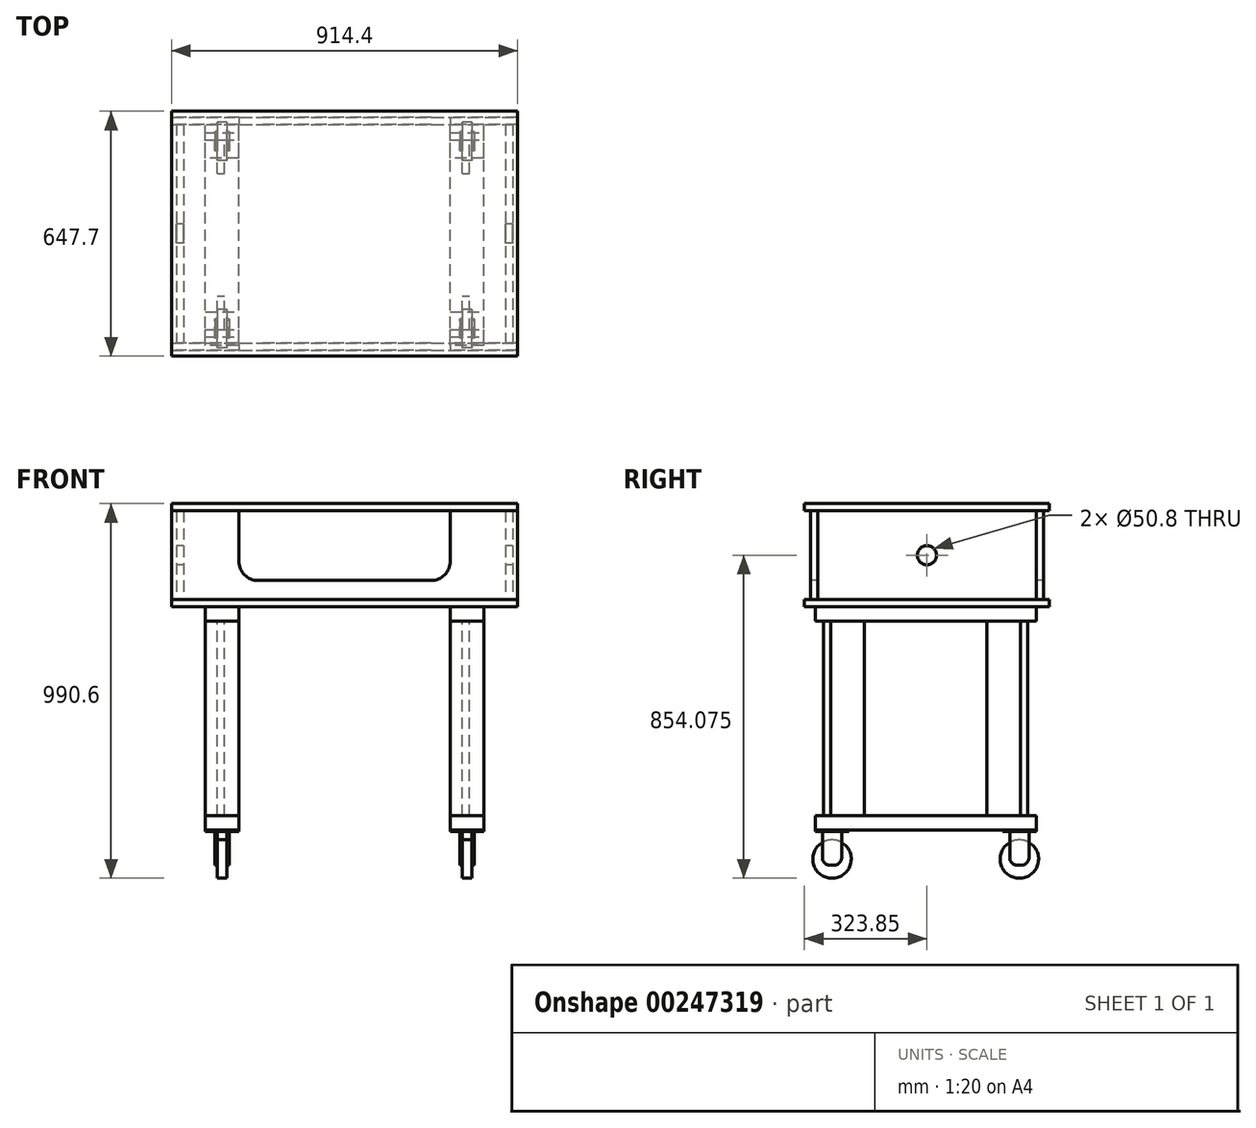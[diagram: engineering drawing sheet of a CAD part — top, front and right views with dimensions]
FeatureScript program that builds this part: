
annotation { "Feature Type Name" : "Feature", "Feature Type Description" : "" }
export const myFeature = defineFeature(function(context is Context, id is Id, definition is map)
    precondition{}
    {
        {
            var Q0;
            Q0=qCreatedBy(makeId("Right.planeOp"),FACE);
            var sketch = newSketch(context, id + "F0", { "sketchPlane" : qUnion([Q0])});
            skLineSegment(sketch, "E0.bottom", {"start": v(0, 0) * mm, "end": v(647.7, 0) * mm});
            skLineSegment(sketch, "E0.top", {"start": v(0, 19.05) * mm, "end": v(647.7, 19.05) * mm});
            skLineSegment(sketch, "E0.left", {"start": v(0, 0) * mm, "end": v(0, 19.05) * mm});
            skLineSegment(sketch, "E0.right", {"start": v(647.7, 0) * mm, "end": v(647.7, 19.05) * mm});
            skSolve(sketch);
        }
        {
            var Q0;
            Q0=makeQuery(id+"F0.imprint","IMPRINT",FACE,{"disambiguationData":[TD([[makeQuery(id+"F0.imprint","IMPRINT",EDGE,{"derivedFrom":sQuery(id+"F0.wireOp",EDGE,"E0.bottom")}),1.0]])]});
            extrude(context, id + "F1", {"entities" : qUnion([Q0]), "oppositeDirection" : true, "depth" : 914.4 * mm});
        }
        {
            var Q0;
            Q0=qCreatedBy(makeId("Top.planeOp"),FACE);
            var sketch = newSketch(context, id + "F2", { "sketchPlane" : qUnion([Q0])});
            skLineSegment(sketch, "E1.bottom", {"start": v(0, 0) * mm, "end": v(-88.9, 0) * mm});
            skLineSegment(sketch, "E1.top", {"start": v(0, 584.2) * mm, "end": v(-88.9, 584.2) * mm});
            skLineSegment(sketch, "E1.left", {"start": v(0, 0) * mm, "end": v(0, 584.2) * mm});
            skLineSegment(sketch, "E1.right", {"start": v(-88.9, 0) * mm, "end": v(-88.9, 584.2) * mm});
            skSolve(sketch);
        }
        {
            var Q0;
            Q0=makeQuery(id+"F2.imprint","IMPRINT",FACE,{"disambiguationData":[TD([[makeQuery(id+"F2.imprint","IMPRINT",EDGE,{"derivedFrom":sQuery(id+"F2.wireOp",EDGE,"E1.bottom")}),-1.0]])]});
            extrude(context, id + "F3", {"entities" : qUnion([Q0]), "oppositeDirection" : true, "depth" : 38.1 * mm});
        }
        {
            var Q0;
            Q0=makeQuery(id+"F3.opExtrude","SWEPT_FACE",FACE,{"disambiguationData":[OSD([sQuery(id+"F2.wireOp",EDGE,"E1.left")])]});
            var sketch = newSketch(context, id + "F4", { "sketchPlane" : qUnion([Q0])});
            skLineSegment(sketch, "E2.bottom", {"start": v(50.8, -38.1) * mm, "end": v(69.85, -38.1) * mm});
            skLineSegment(sketch, "E2.top", {"start": v(50.8, -552.45) * mm, "end": v(69.85, -552.45) * mm});
            skLineSegment(sketch, "E2.left", {"start": v(50.8, -38.1) * mm, "end": v(50.8, -552.45) * mm});
            skLineSegment(sketch, "E2.right", {"start": v(69.85, -38.1) * mm, "end": v(69.85, -552.45) * mm});
            skSolve(sketch);
        }
        {
            var Q0;
            Q0=makeQuery(id+"F4.imprint","IMPRINT",FACE,{"disambiguationData":[TD([[makeQuery(id+"F4.imprint","IMPRINT",EDGE,{"derivedFrom":sQuery(id+"F4.wireOp",EDGE,"E2.bottom")}),-1.0]])]});
            extrude(context, id + "F5", {"entities" : qUnion([Q0]), "oppositeDirection" : true, "depth" : 88.9 * mm});
        }
        {
            var Q0;
            Q0=makeQuery(id+"F5.opExtrude","SWEPT_FACE",FACE,{"disambiguationData":[OSD([sQuery(id+"F4.wireOp",EDGE,"E2.bottom")])]});
            var sketch = newSketch(context, id + "F6", { "sketchPlane" : qUnion([Q0])});
            skLineSegment(sketch, "E3.bottom", {"start": v(-57.48, 69.85) * mm, "end": v(-38.43, 69.85) * mm});
            skLineSegment(sketch, "E3.top", {"start": v(-57.48, 158.75) * mm, "end": v(-38.43, 158.75) * mm});
            skLineSegment(sketch, "E3.left", {"start": v(-57.48, 69.85) * mm, "end": v(-57.48, 158.75) * mm});
            skLineSegment(sketch, "E3.right", {"start": v(-38.43, 69.85) * mm, "end": v(-38.43, 158.75) * mm});
            skSolve(sketch);
        }
        {
            var Q0;
            Q0=makeQuery(id+"F6.imprint","IMPRINT",FACE,{"disambiguationData":[TD([[makeQuery(id+"F6.imprint","IMPRINT",EDGE,{"derivedFrom":sQuery(id+"F6.wireOp",EDGE,"E3.bottom")}),1.0]])]});
            extrude(context, id + "F7", {"entities" : qUnion([Q0]), "oppositeDirection" : true, "depth" : 514.35 * mm});
        }
        {
            var Q0;
            Q0=makeQuery(id+"F5.opExtrude","SWEPT_BODY",BODY,{"disambiguationData":[OSD([sQuery(id+"F4.wireOp",EDGE,"E2.bottom"),sQuery(id+"F4.wireOp",EDGE,"E2.top"),sQuery(id+"F4.wireOp",EDGE,"E2.left"),sQuery(id+"F4.wireOp",EDGE,"E2.right")])]});
            transform(context, id + "F8", {"entities" : qUnion([Q0]), "transformType" : TransformType.TRANSLATION_3D, "dx" : 0 * mm, "dy" : 520.7 * mm, "dz" : 0 * mm, "makeCopy" : true});
        }
        {
            var Q0;
            Q0=makeQuery(id+"F7.opExtrude","SWEPT_BODY",BODY,{"disambiguationData":[OSD([sQuery(id+"F6.wireOp",EDGE,"E3.bottom"),sQuery(id+"F6.wireOp",EDGE,"E3.top"),sQuery(id+"F6.wireOp",EDGE,"E3.left"),sQuery(id+"F6.wireOp",EDGE,"E3.right")])]});
            transform(context, id + "F9", {"entities" : qUnion([Q0]), "transformType" : TransformType.TRANSLATION_3D, "dx" : 0 * mm, "dy" : 412.75 * mm, "dz" : 0 * mm, "makeCopy" : true});
        }
        {
            var Q0;
            Q0=makeQuery(id+"F3.opExtrude","SWEPT_BODY",BODY,{"disambiguationData":[OSD([sQuery(id+"F2.wireOp",EDGE,"E1.bottom"),sQuery(id+"F2.wireOp",EDGE,"E1.top"),sQuery(id+"F2.wireOp",EDGE,"E1.left"),sQuery(id+"F2.wireOp",EDGE,"E1.right")])]});
            transform(context, id + "F10", {"entities" : qUnion([Q0]), "transformType" : TransformType.TRANSLATION_3D, "dx" : -647.7 * mm, "dy" : 0 * mm, "dz" : 0 * mm, "makeCopy" : true});
        }
        {
            var Q0;
            Q0=makeQuery(id+"F5.opExtrude","SWEPT_BODY",BODY,{"disambiguationData":[OSD([sQuery(id+"F4.wireOp",EDGE,"E2.bottom"),sQuery(id+"F4.wireOp",EDGE,"E2.top"),sQuery(id+"F4.wireOp",EDGE,"E2.left"),sQuery(id+"F4.wireOp",EDGE,"E2.right")])]});
            transform(context, id + "F11", {"entities" : qUnion([Q0]), "transformType" : TransformType.TRANSLATION_3D, "dx" : -647.7 * mm, "dy" : 0 * mm, "dz" : 0 * mm, "makeCopy" : true});
        }
        {
            var Q0;
            Q0=makeQuery(id+"F8.opPattern","COPY",BODY,{"derivedFrom":makeQuery(id+"F5.opExtrude","SWEPT_BODY",BODY,{"disambiguationData":[OSD([sQuery(id+"F4.wireOp",EDGE,"E2.bottom"),sQuery(id+"F4.wireOp",EDGE,"E2.top"),sQuery(id+"F4.wireOp",EDGE,"E2.left"),sQuery(id+"F4.wireOp",EDGE,"E2.right")])]}),"instanceName":"1"});
            transform(context, id + "F12", {"entities" : qUnion([Q0]), "transformType" : TransformType.TRANSLATION_3D, "dx" : -647.7 * mm, "dy" : 0 * mm, "dz" : 0 * mm, "makeCopy" : true});
        }
        {
            var Q0;
            Q0=makeQuery(id+"F9.opPattern","COPY",BODY,{"derivedFrom":makeQuery(id+"F7.opExtrude","SWEPT_BODY",BODY,{"disambiguationData":[OSD([sQuery(id+"F6.wireOp",EDGE,"E3.bottom"),sQuery(id+"F6.wireOp",EDGE,"E3.top"),sQuery(id+"F6.wireOp",EDGE,"E3.left"),sQuery(id+"F6.wireOp",EDGE,"E3.right")])]}),"instanceName":"1"});
            transform(context, id + "F13", {"entities" : qUnion([Q0]), "transformType" : TransformType.TRANSLATION_3D, "dx" : -647.7 * mm, "dy" : 0 * mm, "dz" : 0 * mm, "makeCopy" : true});
        }
        {
            var Q0;
            Q0=makeQuery(id+"F7.opExtrude","SWEPT_BODY",BODY,{"disambiguationData":[OSD([sQuery(id+"F6.wireOp",EDGE,"E3.bottom"),sQuery(id+"F6.wireOp",EDGE,"E3.top"),sQuery(id+"F6.wireOp",EDGE,"E3.left"),sQuery(id+"F6.wireOp",EDGE,"E3.right")])]});
            transform(context, id + "F14", {"entities" : qUnion([Q0]), "transformType" : TransformType.TRANSLATION_3D, "dx" : -647.7 * mm, "dy" : 0 * mm, "dz" : 0 * mm, "makeCopy" : true});
        }
        {
            var Q0;
            Q0=makeQuery(id+"F1.opExtrude","SWEPT_BODY",BODY,{"disambiguationData":[OSD([sQuery(id+"F0.wireOp",EDGE,"E0.bottom"),sQuery(id+"F0.wireOp",EDGE,"E0.top"),sQuery(id+"F0.wireOp",EDGE,"E0.left"),sQuery(id+"F0.wireOp",EDGE,"E0.right")])]});
            transform(context, id + "F15", {"entities" : qUnion([Q0]), "transformType" : TransformType.TRANSLATION_3D, "dx" : 88.9 * mm, "dy" : 0 * mm, "dz" : 0 * mm, "makeCopy" : false});
        }
        {
            var Q0;
            Q0=makeQuery(id+"F3.opExtrude","SWEPT_BODY",BODY,{"disambiguationData":[OSD([sQuery(id+"F2.wireOp",EDGE,"E1.bottom"),sQuery(id+"F2.wireOp",EDGE,"E1.top"),sQuery(id+"F2.wireOp",EDGE,"E1.left"),sQuery(id+"F2.wireOp",EDGE,"E1.right")])]});
            transform(context, id + "F16", {"entities" : qUnion([Q0]), "transformType" : TransformType.TRANSLATION_3D, "dx" : 0 * mm, "dy" : 28.57 * mm, "dz" : 0 * mm, "makeCopy" : false});
        }
        {
            var Q0;
            Q0=makeQuery(id+"F10.opPattern","COPY",BODY,{"derivedFrom":makeQuery(id+"F3.opExtrude","SWEPT_BODY",BODY,{"disambiguationData":[OSD([sQuery(id+"F2.wireOp",EDGE,"E1.bottom"),sQuery(id+"F2.wireOp",EDGE,"E1.top"),sQuery(id+"F2.wireOp",EDGE,"E1.left"),sQuery(id+"F2.wireOp",EDGE,"E1.right")])]}),"instanceName":"1"});
            transform(context, id + "F17", {"entities" : qUnion([Q0]), "transformType" : TransformType.TRANSLATION_3D, "dx" : 0 * mm, "dy" : 28.57 * mm, "dz" : 0 * mm, "makeCopy" : false});
        }
        {
            var Q0;
            Q0=makeQuery(id+"F3.opExtrude","SWEPT_BODY",BODY,{"disambiguationData":[OSD([sQuery(id+"F2.wireOp",EDGE,"E1.bottom"),sQuery(id+"F2.wireOp",EDGE,"E1.top"),sQuery(id+"F2.wireOp",EDGE,"E1.left"),sQuery(id+"F2.wireOp",EDGE,"E1.right")])]});
            transform(context, id + "F18", {"entities" : qUnion([Q0]), "transformType" : TransformType.TRANSLATION_3D, "dx" : 0 * mm, "dy" : 0 * mm, "dz" : -673.1 * mm, "makeCopy" : true});
        }
        {
            var Q0;
            Q0=makeQuery(id+"F10.opPattern","COPY",BODY,{"derivedFrom":makeQuery(id+"F3.opExtrude","SWEPT_BODY",BODY,{"disambiguationData":[OSD([sQuery(id+"F2.wireOp",EDGE,"E1.bottom"),sQuery(id+"F2.wireOp",EDGE,"E1.top"),sQuery(id+"F2.wireOp",EDGE,"E1.left"),sQuery(id+"F2.wireOp",EDGE,"E1.right")])]}),"instanceName":"1"});
            transform(context, id + "F19", {"entities" : qUnion([Q0]), "transformType" : TransformType.TRANSLATION_3D, "dx" : 0 * mm, "dy" : 0 * mm, "dz" : -673.1 * mm, "makeCopy" : true});
        }
        {
            var Q0;
            Q0=makeQuery(id+"F19.opPattern","COPY",BODY,{"derivedFrom":makeQuery(id+"F10.opPattern","COPY",BODY,{"derivedFrom":makeQuery(id+"F3.opExtrude","SWEPT_BODY",BODY,{"disambiguationData":[OSD([sQuery(id+"F2.wireOp",EDGE,"E1.bottom"),sQuery(id+"F2.wireOp",EDGE,"E1.top"),sQuery(id+"F2.wireOp",EDGE,"E1.left"),sQuery(id+"F2.wireOp",EDGE,"E1.right")])]}),"instanceName":"1"}),"instanceName":"1"});
            deleteBodies(context, id + "F20", {"entities" : qUnion([Q0])});
        }
        {
            var Q0;
            Q0=makeQuery(id+"F18.opPattern","COPY",BODY,{"derivedFrom":makeQuery(id+"F3.opExtrude","SWEPT_BODY",BODY,{"disambiguationData":[OSD([sQuery(id+"F2.wireOp",EDGE,"E1.bottom"),sQuery(id+"F2.wireOp",EDGE,"E1.top"),sQuery(id+"F2.wireOp",EDGE,"E1.left"),sQuery(id+"F2.wireOp",EDGE,"E1.right")])]}),"instanceName":"1"});
            deleteBodies(context, id + "F21", {"entities" : qUnion([Q0])});
        }
        {
            var Q0;
            Q0=makeQuery(id+"F3.opExtrude","SWEPT_BODY",BODY,{"disambiguationData":[OSD([sQuery(id+"F2.wireOp",EDGE,"E1.bottom"),sQuery(id+"F2.wireOp",EDGE,"E1.top"),sQuery(id+"F2.wireOp",EDGE,"E1.left"),sQuery(id+"F2.wireOp",EDGE,"E1.right")])]});
            transform(context, id + "F22", {"entities" : qUnion([Q0]), "transformType" : TransformType.TRANSLATION_3D, "dx" : 0 * mm, "dy" : 0 * mm, "dz" : -552.45 * mm, "makeCopy" : true});
        }
        {
            var Q0;
            Q0=makeQuery(id+"F10.opPattern","COPY",BODY,{"derivedFrom":makeQuery(id+"F3.opExtrude","SWEPT_BODY",BODY,{"disambiguationData":[OSD([sQuery(id+"F2.wireOp",EDGE,"E1.bottom"),sQuery(id+"F2.wireOp",EDGE,"E1.top"),sQuery(id+"F2.wireOp",EDGE,"E1.left"),sQuery(id+"F2.wireOp",EDGE,"E1.right")])]}),"instanceName":"1"});
            transform(context, id + "F23", {"entities" : qUnion([Q0]), "transformType" : TransformType.TRANSLATION_3D, "dx" : 0 * mm, "dy" : 0 * mm, "dz" : -552.45 * mm, "makeCopy" : true});
        }
        {
            var Q0;
            Q0=makeQuery(id+"F1.opExtrude","SWEPT_BODY",BODY,{"disambiguationData":[OSD([sQuery(id+"F0.wireOp",EDGE,"E0.bottom"),sQuery(id+"F0.wireOp",EDGE,"E0.top"),sQuery(id+"F0.wireOp",EDGE,"E0.left"),sQuery(id+"F0.wireOp",EDGE,"E0.right")])]});
            transform(context, id + "F24", {"entities" : qUnion([Q0]), "transformType" : TransformType.TRANSLATION_3D, "dx" : 0 * mm, "dy" : 0 * mm, "dz" : 254 * mm, "makeCopy" : true});
        }
        {
            var Q0;
            Q0=qCreatedBy(makeId("Front.planeOp"),FACE);
            var sketch = newSketch(context, id + "F25", { "sketchPlane" : qUnion([Q0])});
            skLineSegment(sketch, "E4", {"start": v(0, 0) * mm, "end": v(0, 234.95) * mm});
            skLineSegment(sketch, "E5", {"start": v(0, 234.95) * mm, "end": v(-177.8, 234.95) * mm});
            skLineSegment(sketch, "E6", {"start": v(-177.8, 234.95) * mm, "end": v(-177.8, 101.6) * mm});
            skLineSegment(sketch, "E7", {"start": v(-228.6, 50.8) * mm, "end": v(-685.8, 50.8) * mm});
            skLineSegment(sketch, "E8", {"start": v(-736.6, 101.6) * mm, "end": v(-736.6, 234.95) * mm});
            skLineSegment(sketch, "E9", {"start": v(-736.6, 234.95) * mm, "end": v(-914.4, 234.95) * mm});
            skLineSegment(sketch, "E10", {"start": v(-914.4, 234.95) * mm, "end": v(-914.4, 0) * mm});
            skLineSegment(sketch, "E11", {"start": v(-914.4, 0) * mm, "end": v(0, 0) * mm});
            skPoint(sketch, "E12.visualSharp", {"position": v(-736.6, 50.8) * mm});
            skArc(sketch, "E12.filletArc", {"start": v(-736.6, 101.6) * mm, "mid": v(-721.72, 65.68) * mm, "end": v(-685.8, 50.8) * mm});
            skPoint(sketch, "E13.visualSharp", {"position": v(-177.8, 50.8) * mm});
            skArc(sketch, "E13.filletArc", {"start": v(-228.6, 50.8) * mm, "mid": v(-192.68, 65.68) * mm, "end": v(-177.8, 101.6) * mm});
            skSolve(sketch);
        }
        {
            var Q0;
            Q0=makeQuery(id+"F25.imprint","IMPRINT",FACE,{"disambiguationData":[TD([[makeQuery(id+"F25.imprint","IMPRINT",EDGE,{"derivedFrom":sQuery(id+"F25.wireOp",EDGE,"E4")}),1.0]])]});
            extrude(context, id + "F26", {"entities" : qUnion([Q0]), "oppositeDirection" : true, "depth" : 19.05 * mm});
        }
        {
            var Q0;
            Q0=makeQuery(id+"F26.opExtrude","SWEPT_BODY",BODY,{"disambiguationData":[OSD([sQuery(id+"F25.wireOp",EDGE,"E4"),sQuery(id+"F25.wireOp",EDGE,"E5"),sQuery(id+"F25.wireOp",EDGE,"E6"),sQuery(id+"F25.wireOp",EDGE,"E7"),sQuery(id+"F25.wireOp",EDGE,"E8"),sQuery(id+"F25.wireOp",EDGE,"E9"),sQuery(id+"F25.wireOp",EDGE,"E10"),sQuery(id+"F25.wireOp",EDGE,"E11"),sQuery(id+"F25.wireOp",EDGE,"E12.filletArc"),sQuery(id+"F25.wireOp",EDGE,"E13.filletArc")])]});
            transform(context, id + "F27", {"entities" : qUnion([Q0]), "transformType" : TransformType.TRANSLATION_3D, "dx" : 0 * mm, "dy" : 0 * mm, "dz" : 19.05 * mm, "makeCopy" : false});
        }
        {
            var Q0;
            Q0=makeQuery(id+"F26.opExtrude","SWEPT_BODY",BODY,{"disambiguationData":[OSD([sQuery(id+"F25.wireOp",EDGE,"E4"),sQuery(id+"F25.wireOp",EDGE,"E5"),sQuery(id+"F25.wireOp",EDGE,"E6"),sQuery(id+"F25.wireOp",EDGE,"E7"),sQuery(id+"F25.wireOp",EDGE,"E8"),sQuery(id+"F25.wireOp",EDGE,"E9"),sQuery(id+"F25.wireOp",EDGE,"E10"),sQuery(id+"F25.wireOp",EDGE,"E11"),sQuery(id+"F25.wireOp",EDGE,"E12.filletArc"),sQuery(id+"F25.wireOp",EDGE,"E13.filletArc")])]});
            transform(context, id + "F28", {"entities" : qUnion([Q0]), "transformType" : TransformType.TRANSLATION_3D, "dx" : 88.9 * mm, "dy" : 15.88 * mm, "dz" : 0 * mm, "makeCopy" : false});
        }
        {
            var Q0;
            Q0=makeQuery(id+"F26.opExtrude","SWEPT_BODY",BODY,{"disambiguationData":[OSD([sQuery(id+"F25.wireOp",EDGE,"E4"),sQuery(id+"F25.wireOp",EDGE,"E5"),sQuery(id+"F25.wireOp",EDGE,"E6"),sQuery(id+"F25.wireOp",EDGE,"E7"),sQuery(id+"F25.wireOp",EDGE,"E8"),sQuery(id+"F25.wireOp",EDGE,"E9"),sQuery(id+"F25.wireOp",EDGE,"E10"),sQuery(id+"F25.wireOp",EDGE,"E11"),sQuery(id+"F25.wireOp",EDGE,"E12.filletArc"),sQuery(id+"F25.wireOp",EDGE,"E13.filletArc")])]});
            transform(context, id + "F29", {"entities" : qUnion([Q0]), "transformType" : TransformType.TRANSLATION_3D, "dx" : 0 * mm, "dy" : 596.9 * mm, "dz" : 0 * mm, "makeCopy" : true});
        }
        {
            var Q0;
            Q0=makeQuery(id+"F29.opPattern","COPY",FACE,{"derivedFrom":makeQuery(id+"F26.opExtrude","SWEPT_FACE",FACE,{"disambiguationData":[OSD([sQuery(id+"F25.wireOp",EDGE,"E10")])]}),"instanceName":"1"});
            var sketch = newSketch(context, id + "F30", { "sketchPlane" : qUnion([Q0])});
            skLineSegment(sketch, "E14.bottom", {"start": v(-612.78, 254) * mm, "end": v(-34.92, 254) * mm});
            skLineSegment(sketch, "E14.top", {"start": v(-612.78, 19.05) * mm, "end": v(-34.92, 19.05) * mm});
            skLineSegment(sketch, "E14.left", {"start": v(-612.78, 254) * mm, "end": v(-612.78, 19.05) * mm});
            skLineSegment(sketch, "E14.right", {"start": v(-34.93, 254) * mm, "end": v(-34.92, 19.05) * mm});
            skCircle(sketch, "E15", {"center": v(-323.85, 136.53) * mm, "radius": 25.4 * mm});
            skSolve(sketch);
        }
        {
            var Q0;
            Q0=makeQuery(id+"F30.imprint","IMPRINT",FACE,{"disambiguationData":[TD([[makeQuery(id+"F30.imprint","IMPRINT",EDGE,{"derivedFrom":sQuery(id+"F30.wireOp",EDGE,"E14.bottom")}),-1.0]])]});
            extrude(context, id + "F31", {"entities" : qUnion([Q0]), "oppositeDirection" : true, "depth" : 19.05 * mm});
        }
        {
            var Q0;
            Q0=makeQuery(id+"F31.opExtrude","SWEPT_BODY",BODY,{"disambiguationData":[OSD([sQuery(id+"F30.wireOp",EDGE,"E14.bottom"),sQuery(id+"F30.wireOp",EDGE,"E14.top"),sQuery(id+"F30.wireOp",EDGE,"E14.left"),sQuery(id+"F30.wireOp",EDGE,"E14.right"),sQuery(id+"F30.wireOp",EDGE,"E15")])]});
            transform(context, id + "F32", {"entities" : qUnion([Q0]), "transformType" : TransformType.TRANSLATION_3D, "dx" : 12.7 * mm, "dy" : 0 * mm, "dz" : 0 * mm, "makeCopy" : false});
        }
        {
            var Q0;
            Q0=makeQuery(id+"F31.opExtrude","SWEPT_BODY",BODY,{"disambiguationData":[OSD([sQuery(id+"F30.wireOp",EDGE,"E14.bottom"),sQuery(id+"F30.wireOp",EDGE,"E14.top"),sQuery(id+"F30.wireOp",EDGE,"E14.left"),sQuery(id+"F30.wireOp",EDGE,"E14.right"),sQuery(id+"F30.wireOp",EDGE,"E15")])]});
            transform(context, id + "F33", {"entities" : qUnion([Q0]), "transformType" : TransformType.TRANSLATION_3D, "dx" : 869.95 * mm, "dy" : 0 * mm, "dz" : 0 * mm, "makeCopy" : true});
        }
        {
            var Q0;
            Q0=makeQuery(id+"F23.opPattern","COPY",FACE,{"derivedFrom":makeQuery(id+"F10.opPattern","COPY",FACE,{"derivedFrom":makeQuery(id+"F3.opExtrude","CAP_FACE",FACE,{"disambiguationData":[OSD([sQuery(id+"F2.wireOp",EDGE,"E1.bottom"),sQuery(id+"F2.wireOp",EDGE,"E1.top"),sQuery(id+"F2.wireOp",EDGE,"E1.left"),sQuery(id+"F2.wireOp",EDGE,"E1.right")])],"isStart":false}),"instanceName":"1"}),"instanceName":"1"});
            var sketch = newSketch(context, id + "F34", { "sketchPlane" : qUnion([Q0])});
            skLineSegment(sketch, "E16.bottom", {"start": v(-736.6, -28.58) * mm, "end": v(-647.7, -28.58) * mm});
            skLineSegment(sketch, "E16.top", {"start": v(-736.6, -117.48) * mm, "end": v(-647.7, -117.48) * mm});
            skLineSegment(sketch, "E16.left", {"start": v(-736.6, -28.58) * mm, "end": v(-736.6, -117.48) * mm});
            skLineSegment(sketch, "E16.right", {"start": v(-647.7, -28.58) * mm, "end": v(-647.7, -117.48) * mm});
            skSolve(sketch);
        }
        {
            var Q0;
            Q0=makeQuery(id+"F34.imprint","IMPRINT",FACE,{"disambiguationData":[TD([[makeQuery(id+"F34.imprint","IMPRINT",EDGE,{"derivedFrom":sQuery(id+"F34.wireOp",EDGE,"E16.bottom")}),1.0]])]});
            extrude(context, id + "F35", {"entities" : qUnion([Q0]), "depth" : 3.17 * mm});
        }
        {
            var Q0;
            Q0=makeQuery(id+"F23.opPattern","COPY",FACE,{"derivedFrom":makeQuery(id+"F10.opPattern","COPY",FACE,{"derivedFrom":makeQuery(id+"F3.opExtrude","SWEPT_FACE",FACE,{"disambiguationData":[OSD([sQuery(id+"F2.wireOp",EDGE,"E1.right")])]}),"instanceName":"1"}),"instanceName":"1"});
            var sketch = newSketch(context, id + "F36", { "sketchPlane" : qUnion([Q0])});
            skLineSegment(sketch, "E17", {"start": v(-28.58, -590.55) * mm, "end": v(-73.03, -590.55) * mm});
            skLineSegment(sketch, "E18", {"start": v(-73.03, -590.55) * mm, "end": v(-73.03, -666.75) * mm});
            skCircle(sketch, "E19", {"center": v(-73.03, -666.75) * mm, "radius": 50.8 * mm});
            skSolve(sketch);
        }
        {
            var Q0;
            Q0=makeQuery(id+"F36.imprint","IMPRINT",FACE,{"disambiguationData":[TD([[makeQuery(id+"F36.imprint","IMPRINT",EDGE,{"derivedFrom":sQuery(id+"F36.wireOp",EDGE,"E19")}),1.0]])]});
            extrude(context, id + "F37", {"entities" : qUnion([Q0]), "oppositeDirection" : true, "depth" : 25.4 * mm});
        }
        {
            var Q0;
            Q0=makeQuery(id+"F37.opExtrude","SWEPT_BODY",BODY,{"disambiguationData":[OSD([sQuery(id+"F36.wireOp",EDGE,"E19")])]});
            transform(context, id + "F38", {"entities" : qUnion([Q0]), "transformType" : TransformType.TRANSLATION_3D, "dx" : 31.75 * mm, "dy" : 0 * mm, "dz" : 0 * mm, "makeCopy" : false});
        }
        {
            var Q0;
            Q0=makeQuery(id+"F35.opExtrude","SWEPT_FACE",FACE,{"disambiguationData":[OSD([sQuery(id+"F34.wireOp",EDGE,"E16.left")])]});
            var sketch = newSketch(context, id + "F39", { "sketchPlane" : qUnion([Q0])});
            skLineSegment(sketch, "E20.bottom", {"start": v(-117.48, -593.73) * mm, "end": v(-66.68, -593.73) * mm});
            skLineSegment(sketch, "E20.top", {"start": v(-98.43, -682.63) * mm, "end": v(-85.73, -682.63) * mm});
            skLineSegment(sketch, "E20.left", {"start": v(-117.48, -593.73) * mm, "end": v(-117.48, -663.58) * mm});
            skLineSegment(sketch, "E20.right", {"start": v(-66.68, -593.73) * mm, "end": v(-66.68, -663.58) * mm});
            skPoint(sketch, "E21.visualSharp", {"position": v(-117.48, -682.63) * mm});
            skArc(sketch, "E21.filletArc", {"start": v(-117.48, -663.58) * mm, "mid": v(-111.9, -677.05) * mm, "end": v(-98.43, -682.63) * mm});
            skPoint(sketch, "E22.visualSharp", {"position": v(-66.68, -682.63) * mm});
            skArc(sketch, "E22.filletArc", {"start": v(-85.73, -682.63) * mm, "mid": v(-72.25, -677.05) * mm, "end": v(-66.68, -663.58) * mm});
            skSolve(sketch);
        }
        {
            var Q0;
            Q0=makeQuery(id+"F39.imprint","IMPRINT",FACE,{"disambiguationData":[TD([[makeQuery(id+"F39.imprint","IMPRINT",EDGE,{"derivedFrom":sQuery(id+"F39.wireOp",EDGE,"E20.bottom")}),1.0]])]});
            extrude(context, id + "F40", {"entities" : qUnion([Q0]), "oppositeDirection" : true, "depth" : 6.35 * mm});
        }
        {
            var Q0;
            Q0=makeQuery(id+"F40.opExtrude","SWEPT_BODY",BODY,{"disambiguationData":[OSD([sQuery(id+"F39.wireOp",EDGE,"E20.bottom"),sQuery(id+"F39.wireOp",EDGE,"E20.top"),sQuery(id+"F39.wireOp",EDGE,"E20.left"),sQuery(id+"F39.wireOp",EDGE,"E20.right"),sQuery(id+"F39.wireOp",EDGE,"E21.filletArc"),sQuery(id+"F39.wireOp",EDGE,"E22.filletArc")])]});
            transform(context, id + "F41", {"entities" : qUnion([Q0]), "transformType" : TransformType.TRANSLATION_3D, "dx" : 25.4 * mm, "dy" : 0 * mm, "dz" : 0 * mm, "makeCopy" : false});
        }
        {
            var Q0;
            Q0=makeQuery(id+"F40.opExtrude","SWEPT_BODY",BODY,{"disambiguationData":[OSD([sQuery(id+"F39.wireOp",EDGE,"E20.bottom"),sQuery(id+"F39.wireOp",EDGE,"E20.top"),sQuery(id+"F39.wireOp",EDGE,"E20.left"),sQuery(id+"F39.wireOp",EDGE,"E20.right"),sQuery(id+"F39.wireOp",EDGE,"E21.filletArc"),sQuery(id+"F39.wireOp",EDGE,"E22.filletArc")])]});
            transform(context, id + "F42", {"entities" : qUnion([Q0]), "transformType" : TransformType.TRANSLATION_3D, "dx" : 31.75 * mm, "dy" : -19.05 * mm, "dz" : 0 * mm, "makeCopy" : true});
        }
        {
            var Q0;
            Q0=makeQuery(id+"F40.opExtrude","SWEPT_BODY",BODY,{"disambiguationData":[OSD([sQuery(id+"F39.wireOp",EDGE,"E20.bottom"),sQuery(id+"F39.wireOp",EDGE,"E20.top"),sQuery(id+"F39.wireOp",EDGE,"E20.left"),sQuery(id+"F39.wireOp",EDGE,"E20.right"),sQuery(id+"F39.wireOp",EDGE,"E21.filletArc"),sQuery(id+"F39.wireOp",EDGE,"E22.filletArc")])]});
            transform(context, id + "F43", {"entities" : qUnion([Q0]), "transformType" : TransformType.TRANSLATION_3D, "dx" : 0 * mm, "dy" : -19.05 * mm, "dz" : 0 * mm, "makeCopy" : false});
        }
        {
            var Q0;
            Q0=makeQuery(id+"F35.opExtrude","SWEPT_BODY",BODY,{"disambiguationData":[OSD([sQuery(id+"F34.wireOp",EDGE,"E16.bottom"),sQuery(id+"F34.wireOp",EDGE,"E16.top"),sQuery(id+"F34.wireOp",EDGE,"E16.left"),sQuery(id+"F34.wireOp",EDGE,"E16.right")])]});
            transform(context, id + "F44", {"entities" : qUnion([Q0]), "transformType" : TransformType.TRANSLATION_3D, "dx" : 647.7 * mm, "dy" : 0 * mm, "dz" : 0 * mm, "makeCopy" : true});
        }
        {
            var Q0;
            Q0=makeQuery(id+"F37.opExtrude","SWEPT_BODY",BODY,{"disambiguationData":[OSD([sQuery(id+"F36.wireOp",EDGE,"E19")])]});
            var Q1;
            Q1=makeQuery(id+"F40.opExtrude","SWEPT_BODY",BODY,{"disambiguationData":[OSD([sQuery(id+"F39.wireOp",EDGE,"E20.bottom"),sQuery(id+"F39.wireOp",EDGE,"E20.top"),sQuery(id+"F39.wireOp",EDGE,"E20.left"),sQuery(id+"F39.wireOp",EDGE,"E20.right"),sQuery(id+"F39.wireOp",EDGE,"E21.filletArc"),sQuery(id+"F39.wireOp",EDGE,"E22.filletArc")])]});
            var Q2;
            Q2=makeQuery(id+"F42.opPattern","COPY",BODY,{"derivedFrom":makeQuery(id+"F40.opExtrude","SWEPT_BODY",BODY,{"disambiguationData":[OSD([sQuery(id+"F39.wireOp",EDGE,"E20.bottom"),sQuery(id+"F39.wireOp",EDGE,"E20.top"),sQuery(id+"F39.wireOp",EDGE,"E20.left"),sQuery(id+"F39.wireOp",EDGE,"E20.right"),sQuery(id+"F39.wireOp",EDGE,"E21.filletArc"),sQuery(id+"F39.wireOp",EDGE,"E22.filletArc")])]}),"instanceName":"1"});
            transform(context, id + "F45", {"entities" : qUnion([Q0, Q1, Q2]), "transformType" : TransformType.TRANSLATION_3D, "dx" : 647.7 * mm, "dy" : 0 * mm, "dz" : 0 * mm, "makeCopy" : true});
        }
        {
            var Q0;
            Q0=makeQuery(id+"F35.opExtrude","SWEPT_BODY",BODY,{"disambiguationData":[OSD([sQuery(id+"F34.wireOp",EDGE,"E16.bottom"),sQuery(id+"F34.wireOp",EDGE,"E16.top"),sQuery(id+"F34.wireOp",EDGE,"E16.left"),sQuery(id+"F34.wireOp",EDGE,"E16.right")])]});
            var Q1;
            Q1=makeQuery(id+"F45.opPattern","COPY",BODY,{"derivedFrom":makeQuery(id+"F40.opExtrude","SWEPT_BODY",BODY,{"disambiguationData":[OSD([sQuery(id+"F39.wireOp",EDGE,"E20.bottom"),sQuery(id+"F39.wireOp",EDGE,"E20.top"),sQuery(id+"F39.wireOp",EDGE,"E20.left"),sQuery(id+"F39.wireOp",EDGE,"E20.right"),sQuery(id+"F39.wireOp",EDGE,"E21.filletArc"),sQuery(id+"F39.wireOp",EDGE,"E22.filletArc")])]}),"instanceName":"1"});
            var Q2;
            Q2=makeQuery(id+"F45.opPattern","COPY",BODY,{"derivedFrom":makeQuery(id+"F37.opExtrude","SWEPT_BODY",BODY,{"disambiguationData":[OSD([sQuery(id+"F36.wireOp",EDGE,"E19")])]}),"instanceName":"1"});
            var Q3;
            Q3=makeQuery(id+"F40.opExtrude","SWEPT_BODY",BODY,{"disambiguationData":[OSD([sQuery(id+"F39.wireOp",EDGE,"E20.bottom"),sQuery(id+"F39.wireOp",EDGE,"E20.top"),sQuery(id+"F39.wireOp",EDGE,"E20.left"),sQuery(id+"F39.wireOp",EDGE,"E20.right"),sQuery(id+"F39.wireOp",EDGE,"E21.filletArc"),sQuery(id+"F39.wireOp",EDGE,"E22.filletArc")])]});
            var Q4;
            Q4=makeQuery(id+"F42.opPattern","COPY",BODY,{"derivedFrom":makeQuery(id+"F40.opExtrude","SWEPT_BODY",BODY,{"disambiguationData":[OSD([sQuery(id+"F39.wireOp",EDGE,"E20.bottom"),sQuery(id+"F39.wireOp",EDGE,"E20.top"),sQuery(id+"F39.wireOp",EDGE,"E20.left"),sQuery(id+"F39.wireOp",EDGE,"E20.right"),sQuery(id+"F39.wireOp",EDGE,"E21.filletArc"),sQuery(id+"F39.wireOp",EDGE,"E22.filletArc")])]}),"instanceName":"1"});
            var Q5;
            Q5=makeQuery(id+"F37.opExtrude","SWEPT_BODY",BODY,{"disambiguationData":[OSD([sQuery(id+"F36.wireOp",EDGE,"E19")])]});
            var Q6;
            Q6=makeQuery(id+"F44.opPattern","COPY",BODY,{"derivedFrom":makeQuery(id+"F35.opExtrude","SWEPT_BODY",BODY,{"disambiguationData":[OSD([sQuery(id+"F34.wireOp",EDGE,"E16.bottom"),sQuery(id+"F34.wireOp",EDGE,"E16.top"),sQuery(id+"F34.wireOp",EDGE,"E16.left"),sQuery(id+"F34.wireOp",EDGE,"E16.right")])]}),"instanceName":"1"});
            var Q7;
            Q7=makeQuery(id+"F45.opPattern","COPY",BODY,{"derivedFrom":makeQuery(id+"F42.opPattern","COPY",BODY,{"derivedFrom":makeQuery(id+"F40.opExtrude","SWEPT_BODY",BODY,{"disambiguationData":[OSD([sQuery(id+"F39.wireOp",EDGE,"E20.bottom"),sQuery(id+"F39.wireOp",EDGE,"E20.top"),sQuery(id+"F39.wireOp",EDGE,"E20.left"),sQuery(id+"F39.wireOp",EDGE,"E20.right"),sQuery(id+"F39.wireOp",EDGE,"E21.filletArc"),sQuery(id+"F39.wireOp",EDGE,"E22.filletArc")])]}),"instanceName":"1"}),"instanceName":"1"});
            transform(context, id + "F46", {"entities" : qUnion([Q0, Q1, Q2, Q3, Q4, Q5, Q6, Q7]), "transformType" : TransformType.TRANSLATION_3D, "dx" : 0 * mm, "dy" : 495.3 * mm, "dz" : 0 * mm, "makeCopy" : true});
        }
    });
